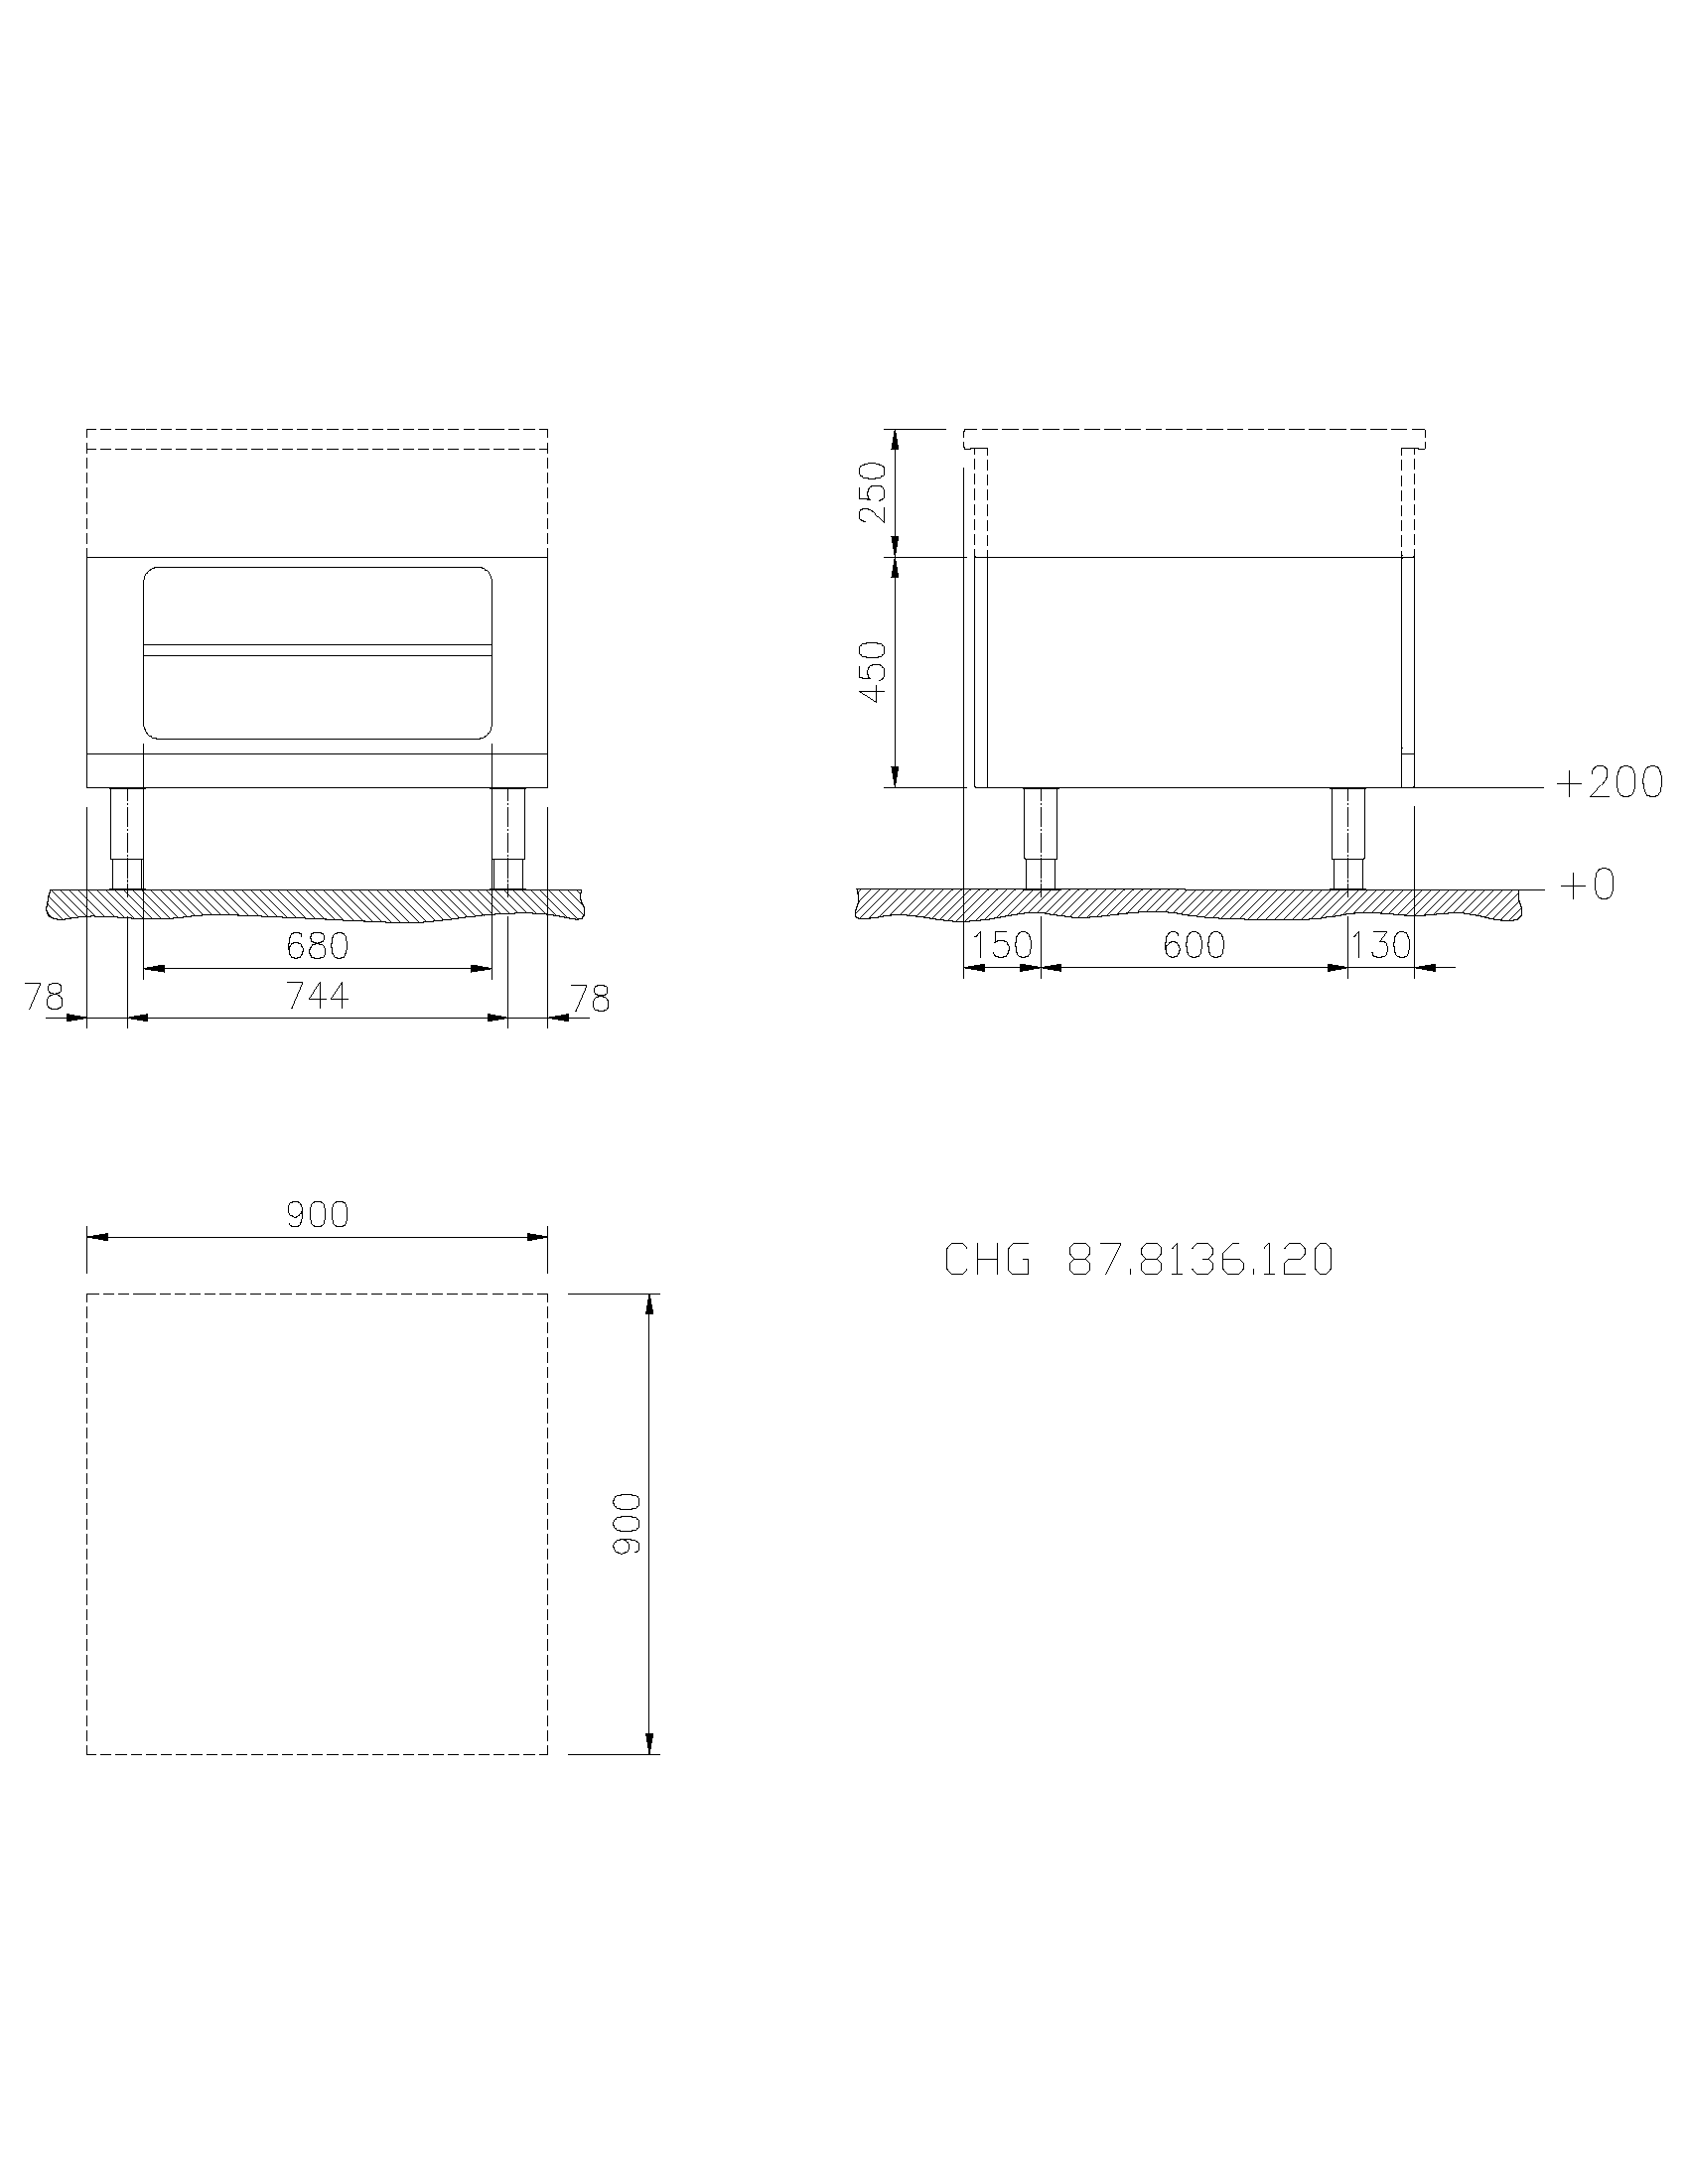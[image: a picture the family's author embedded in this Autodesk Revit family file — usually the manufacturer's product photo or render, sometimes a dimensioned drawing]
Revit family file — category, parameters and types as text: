
# Revit family: QF_ELECTROLUXPROFESSIONAL_589806_MC1HCAFOOM
name_source: partatom
category: Attrezzature speciali
units: mm (PartAtom-declared; Revit-internal decimal feet)

## family parameters
Basato su piano di lavoro = No
Condiviso = No
Punto di calcolo locali = No
Quota connettore circolare = Usa diametro
Sempre verticale = Sì
Taglio con vuoti quando caricato = No
Tipo di parte = Normale

## types (1)
- Standard
    Accessory = Sì
    Cold Water Size = 0"
    Compressed Air Pressure = 0.00 psi
    Compressed Air Size = 0"
    Compressed Air Volume = 0 GPM
    Condensate Return Size = 0"
    Cycle = 0 Hz
    Depth Actual = 900 mm  [stored 2.95276 ft]
    Descrizione = OPEN BASE,H3,GN,1S,700X900X450 MARINE
    Direct Waste Size = 0"
    Gas Input Pressure = 0.0
    Gas KW = 0
    Gas Size = 0"
    HP = 0 HP
    Height Actual = 450 mm  [stored 1.47638 ft]
    Hot Water Size = 0"
    Item Number = 589807
    Length Actual = 700 mm  [stored 2.29659 ft]
    Modello = MC1HCAGOOM
    Phase = 0
    Produttore = Electrolux Professional
    Prospetto di default = 0 mm  [stored 0 ft]
    Refrigerant Compressor Remote = Sì
    Refrigeration Liquid Line Size = 0 mm  [stored 0 ft]
    Refrigeration Suction Line Size = 0 mm  [stored 0 ft]
    Steam Consumption per Hour = 0
    Steam Supply Maximum Pressure = 0.00 psi
    Steam Supply Minimum Pressure = 0.00 psi
    Steam Supply Size = 0"
    URL = https://www.electroluxprofessional.com
    URL Manufacturer = https://www.electroluxprofessional.com
    Volts = 0 V
    Watts = 0 W
    Weight = 21.00 kg

note: source unit labels omitted for Gas Input Pressure — the stored unit's dimension contradicts the parameter name (converter mislabeling)

note: [stored X ft] marks values corroborated as IEEE doubles in the binary element streams (Revit-internal decimal feet)

## geometry (parser evidence)
native form markers: Sweep x3
no freeform markers — native parametric forms only
